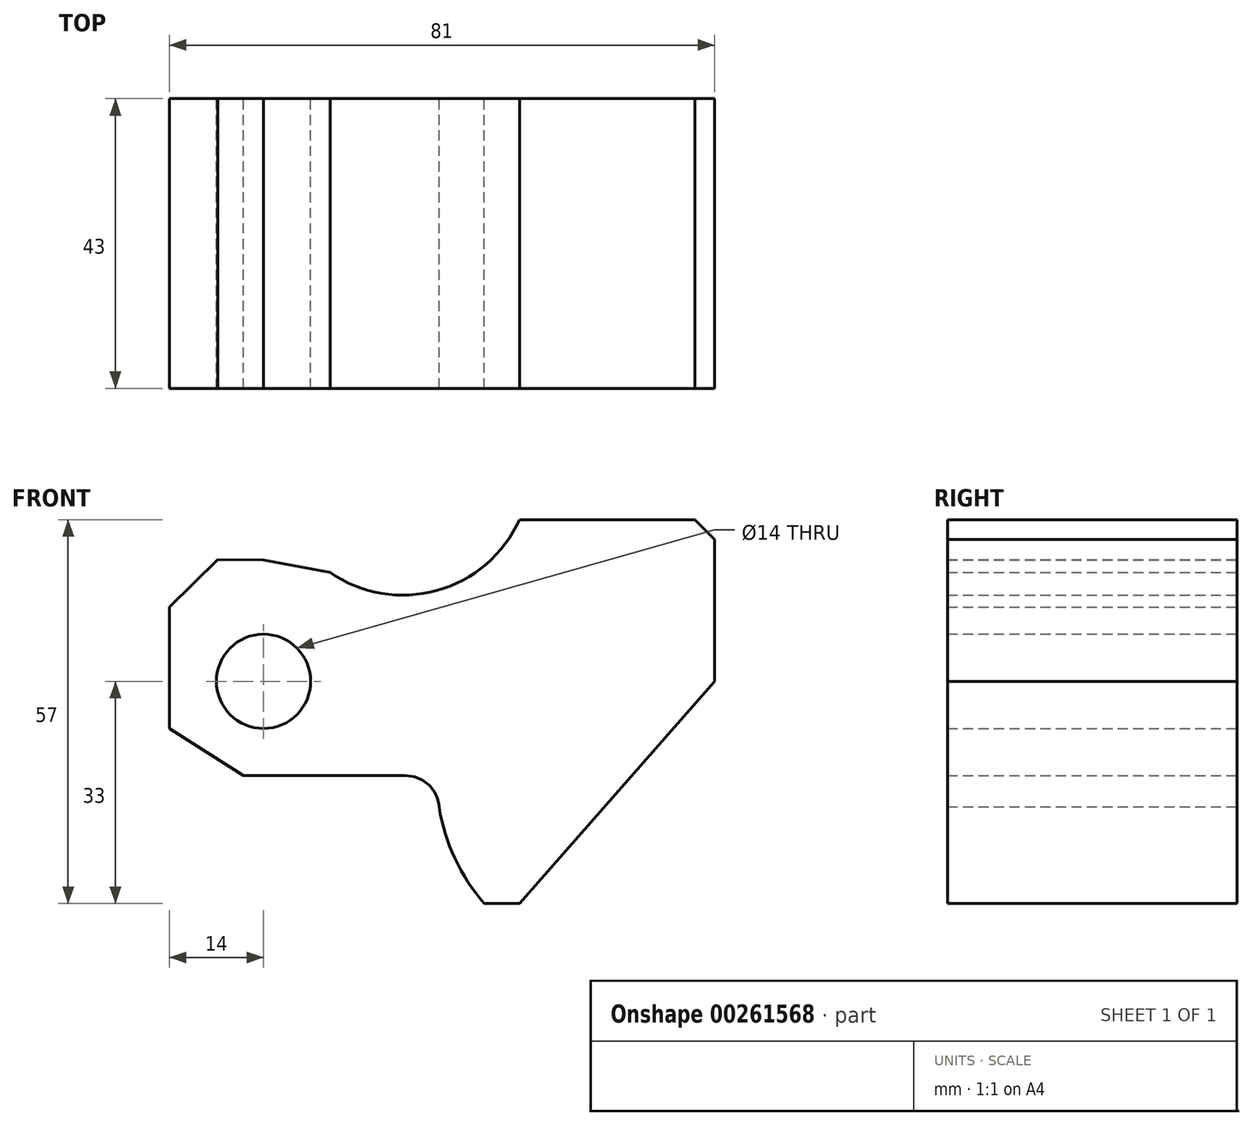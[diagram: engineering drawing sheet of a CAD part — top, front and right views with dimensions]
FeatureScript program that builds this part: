
annotation { "Feature Type Name" : "Feature", "Feature Type Description" : "" }
export const myFeature = defineFeature(function(context is Context, id is Id, definition is map)
    precondition{}
    {
        {
            var Q0;
            Q0=qCreatedBy(makeId("Front.planeOp"),FACE);
            var sketch = newSketch(context, id + "F0", { "sketchPlane" : qUnion([Q0])});
            skCircle(sketch, "E0", {"center": v(0, 0) * mm, "radius": 7 * mm});
            skLineSegment(sketch, "E1", {"start": v(-14, -7) * mm, "end": v(-3, -14) * mm});
            skLineSegment(sketch, "E2", {"start": v(0, 18) * mm, "end": v(0, 18) * mm});
            skLineSegment(sketch, "E3", {"start": v(38, -33) * mm, "end": v(67, 0) * mm});
            skLineSegment(sketch, "E4", {"start": v(67, 0) * mm, "end": v(67, 21.09) * mm});
            skLineSegment(sketch, "E5", {"start": v(-14, 11) * mm, "end": v(-14, -7) * mm});
            skLineSegment(sketch, "E6", {"start": v(-14, 11) * mm, "end": v(-6.8, 18.06) * mm});
            skLineSegment(sketch, "E7", {"start": v(-6.8, 18.06) * mm, "end": v(0, 18) * mm});
            skLineSegment(sketch, "E8", {"start": v(-6.8, 18.06) * mm, "end": v(-14.1, 18.13) * mm});
            skLineSegment(sketch, "E9", {"start": v(0, 18) * mm, "end": v(9.87, 16.16) * mm});
            skLineSegment(sketch, "E10", {"start": v(67, 21.09) * mm, "end": v(64.09, 24) * mm});
            skLineSegment(sketch, "E11", {"start": v(64.09, 24) * mm, "end": v(38, 24) * mm});
            skArc(sketch, "E12", {"start": v(9.87, 16.16) * mm, "mid": v(25.77, 13.5) * mm, "end": v(38, 24) * mm});
            skLineSegment(sketch, "E13", {"start": v(64.09, 24) * mm, "end": v(72.1, 24) * mm});
            skLineSegment(sketch, "E14", {"start": v(0, 18) * mm, "end": v(6.97, 17.93) * mm});
            skLineSegment(sketch, "E15", {"start": v(-3, -14) * mm, "end": v(21.08, -14) * mm});
            skArc(sketch, "E16", {"start": v(26.07, -18.65) * mm, "mid": v(24.5, -15.34) * mm, "end": v(21.08, -14) * mm});
            skLineSegment(sketch, "E17", {"start": v(21.08, -14) * mm, "end": v(54.7, -14) * mm});
            skLineSegment(sketch, "E18", {"start": v(38, -33) * mm, "end": v(32.79, -33) * mm});
            skArc(sketch, "E19", {"start": v(26.07, -18.65) * mm, "mid": v(28.43, -26.3) * mm, "end": v(32.79, -33) * mm});
            skSolve(sketch);
        }
        {
            var Q0;
            Q0=makeQuery(id+"F0.imprint","IMPRINT",FACE,{"disambiguationData":[TD([[makeQuery(id+"F0.imprint","IMPRINT",EDGE,{"derivedFrom":sQuery(id+"F0.wireOp",EDGE,"E0")}),-1.0]])]});
            var Q1;
            Q1=makeQuery(id+"F0.imprint","IMPRINT",FACE,{"disambiguationData":[TD([[makeQuery(id+"F0.imprint","IMPRINT",EDGE,{"derivedFrom":sQuery(id+"F0.wireOp",EDGE,"E16")}),-1.0]])]});
            extrude(context, id + "F1", {"entities" : qUnion([Q0, Q1]), "depth" : 43 * mm});
        }
    });
